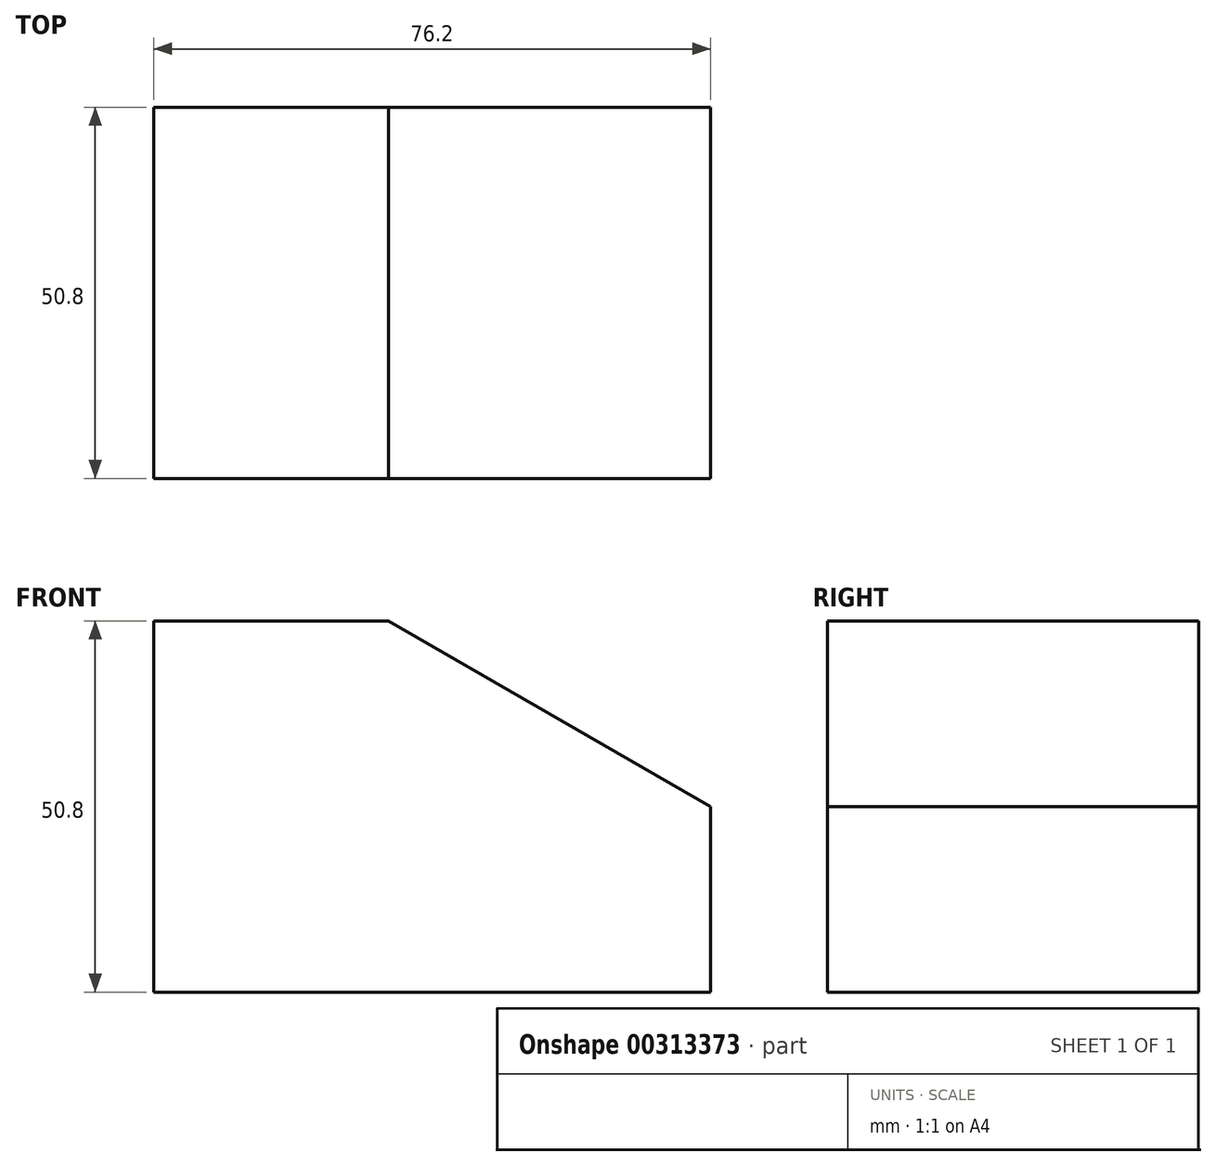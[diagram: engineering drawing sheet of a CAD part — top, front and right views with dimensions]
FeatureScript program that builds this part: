
annotation { "Feature Type Name" : "Feature", "Feature Type Description" : "" }
export const myFeature = defineFeature(function(context is Context, id is Id, definition is map)
    precondition{}
    {
        {
            var Q0;
            Q0=qCreatedBy(makeId("Front.planeOp"),FACE);
            var sketch = newSketch(context, id + "F0", { "sketchPlane" : qUnion([Q0])});
            skLineSegment(sketch, "E0", {"start": v(-32.12, -50.8) * mm, "end": v(44.08, -50.8) * mm});
            skLineSegment(sketch, "E1", {"start": v(-32.12, -50.8) * mm, "end": v(-32.12, 0) * mm});
            skLineSegment(sketch, "E2", {"start": v(-35.96, 0) * mm, "end": v(2.14, 0) * mm});
            skLineSegment(sketch, "E3", {"start": v(44.08, -50.8) * mm, "end": v(44.08, -25.4) * mm});
            skLineSegment(sketch, "E4", {"start": v(0, 0) * mm, "end": v(44.08, -25.4) * mm});
            skSolve(sketch);
        }
        {
            var Q0;
            Q0=makeQuery(id+"F0.imprint","IMPRINT",FACE,{"disambiguationData":[TD([[makeQuery(id+"F0.imprint","IMPRINT",EDGE,{"derivedFrom":sQuery(id+"F0.wireOp",EDGE,"E0")}),1.0]])]});
            extrude(context, id + "F1", {"entities" : qUnion([Q0]), "depth" : 50.8 * mm});
        }
    });
